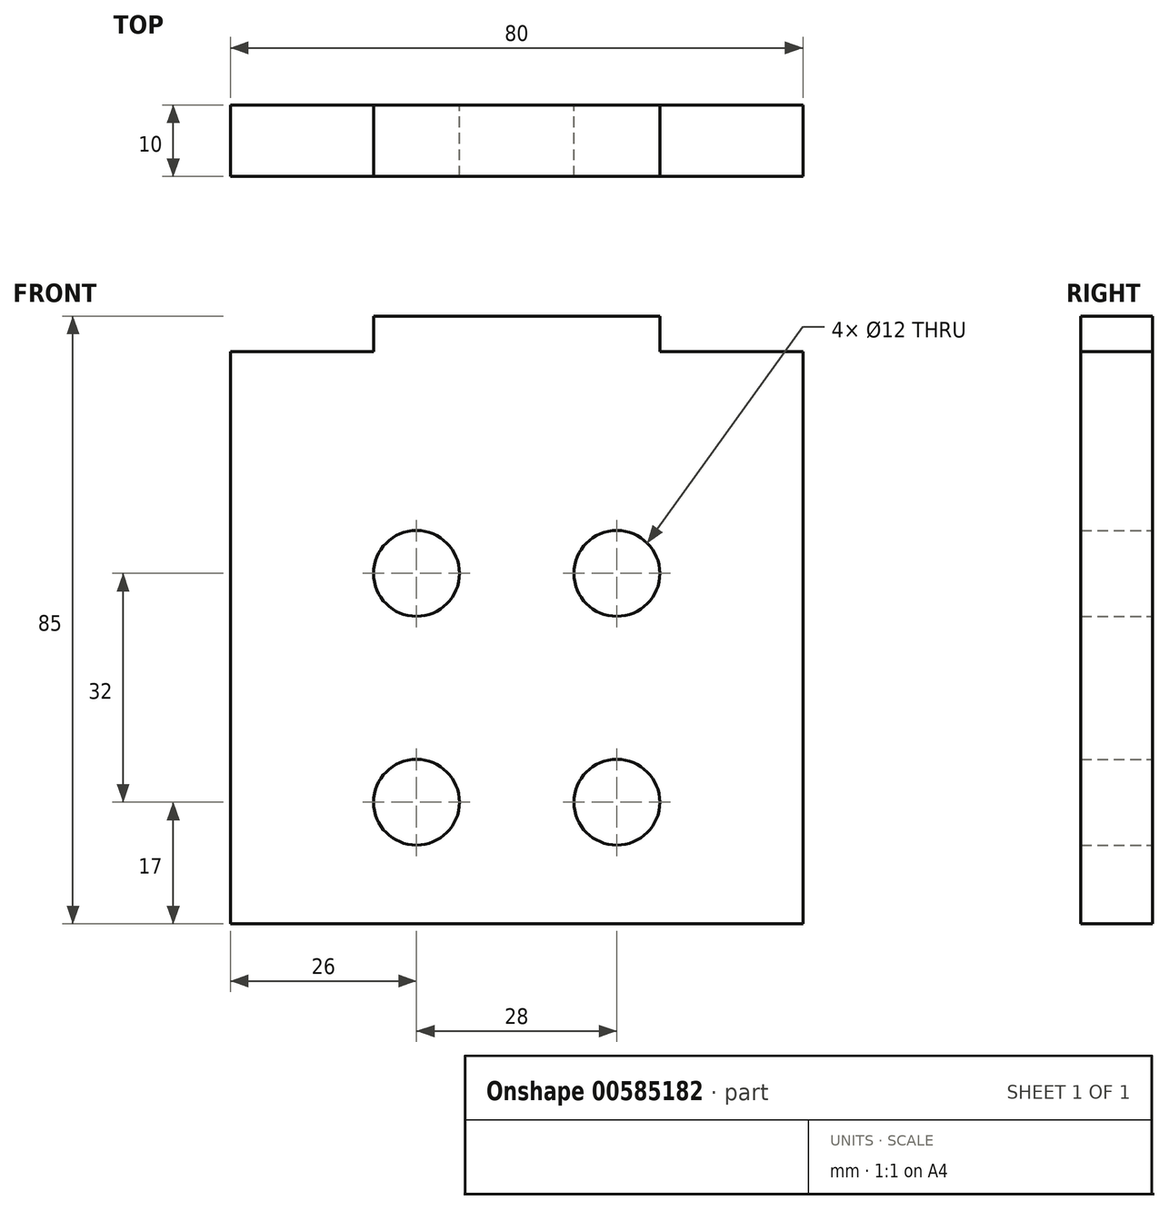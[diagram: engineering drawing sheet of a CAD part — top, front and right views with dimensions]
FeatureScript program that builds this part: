
annotation { "Feature Type Name" : "Feature", "Feature Type Description" : "" }
export const myFeature = defineFeature(function(context is Context, id is Id, definition is map)
    precondition{}
    {
        {
            var Q0;
            Q0=qCreatedBy(makeId("Front.planeOp"),FACE);
            var sketch = newSketch(context, id + "F0", { "sketchPlane" : qUnion([Q0])});
            skLineSegment(sketch, "E0.bottom", {"start": v(0, 0) * mm, "end": v(80, 0) * mm});
            skLineSegment(sketch, "E0.top", {"start": v(0, 80) * mm, "end": v(80, 80) * mm});
            skLineSegment(sketch, "E0.left", {"start": v(0, 0) * mm, "end": v(0, 80) * mm});
            skLineSegment(sketch, "E0.right", {"start": v(80, 0) * mm, "end": v(80, 80) * mm});
            skLineSegment(sketch, "E1.bottom", {"start": v(20, 80) * mm, "end": v(60, 80) * mm});
            skLineSegment(sketch, "E1.top", {"start": v(20, 85) * mm, "end": v(60, 85) * mm});
            skLineSegment(sketch, "E1.left", {"start": v(20, 80) * mm, "end": v(20, 85) * mm});
            skLineSegment(sketch, "E1.right", {"start": v(60, 80) * mm, "end": v(60, 85) * mm});
            skPoint(sketch, "E2", {"position": v(40, 0) * mm});
            skPoint(sketch, "E3", {"position": v(40, 85) * mm});
            skCircle(sketch, "E4", {"center": v(26, 49) * mm, "radius": 6 * mm});
            skCircle(sketch, "E5", {"center": v(54, 49) * mm, "radius": 6 * mm});
            skCircle(sketch, "E6", {"center": v(26, 17) * mm, "radius": 6 * mm});
            skCircle(sketch, "E7", {"center": v(54, 17) * mm, "radius": 6 * mm});
            skLineSegment(sketch, "E8", {"start": v(26, 49) * mm, "end": v(54, 49) * mm, "construction": true});
            skPoint(sketch, "E9", {"position": v(40, 49) * mm});
            skSolve(sketch);
        }
        {
            var Q0;
            Q0 = qSketchRegion(id + "F0", true);
            extrude(context, id + "F1", {"entities" : qUnion([Q0]), "depth" : 10 * mm, "offsetDistance" : 25 * mm});
        }
    });
